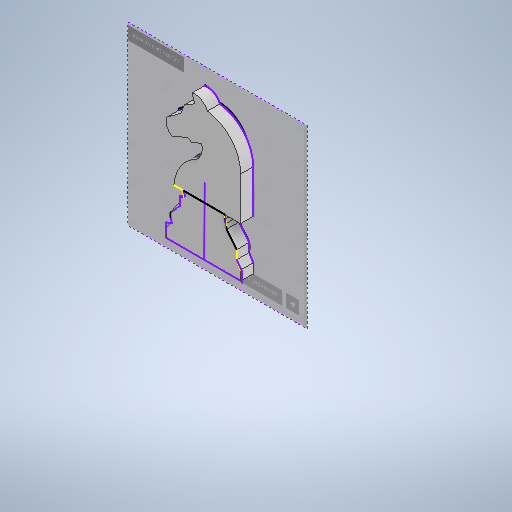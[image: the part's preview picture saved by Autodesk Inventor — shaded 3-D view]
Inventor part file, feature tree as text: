
AUTODESK INVENTOR PART (.ipt)
format: ipt  version: 2025.1 (Build 291241000, 241)  size: 386,048 bytes
history: native  units: mm
features: sketch x3, other x2, extrude x1
ambient origin geometry x8: Origin, YZ Plane, XZ Plane, XY Plane, X Axis, Y Axis, Z Axis, Center Point
bodies: Body1 (feature_tree)
feature tree (6):
  other  "Sólido1"
  sketch  "Boceto1"  dims[d7=10.0mm d8=0.0mm]
  extrude  "Extrusión1"  [1 undecoded]
  sketch  "Boceto3"
  other  "Imagen1"
  sketch  "Boceto2"
note: 1 required parameter value undecoded (feature->parameter linkage not recoverable at this tier; creation-order binding heuristic only, values carry confidence <= 0.55)
